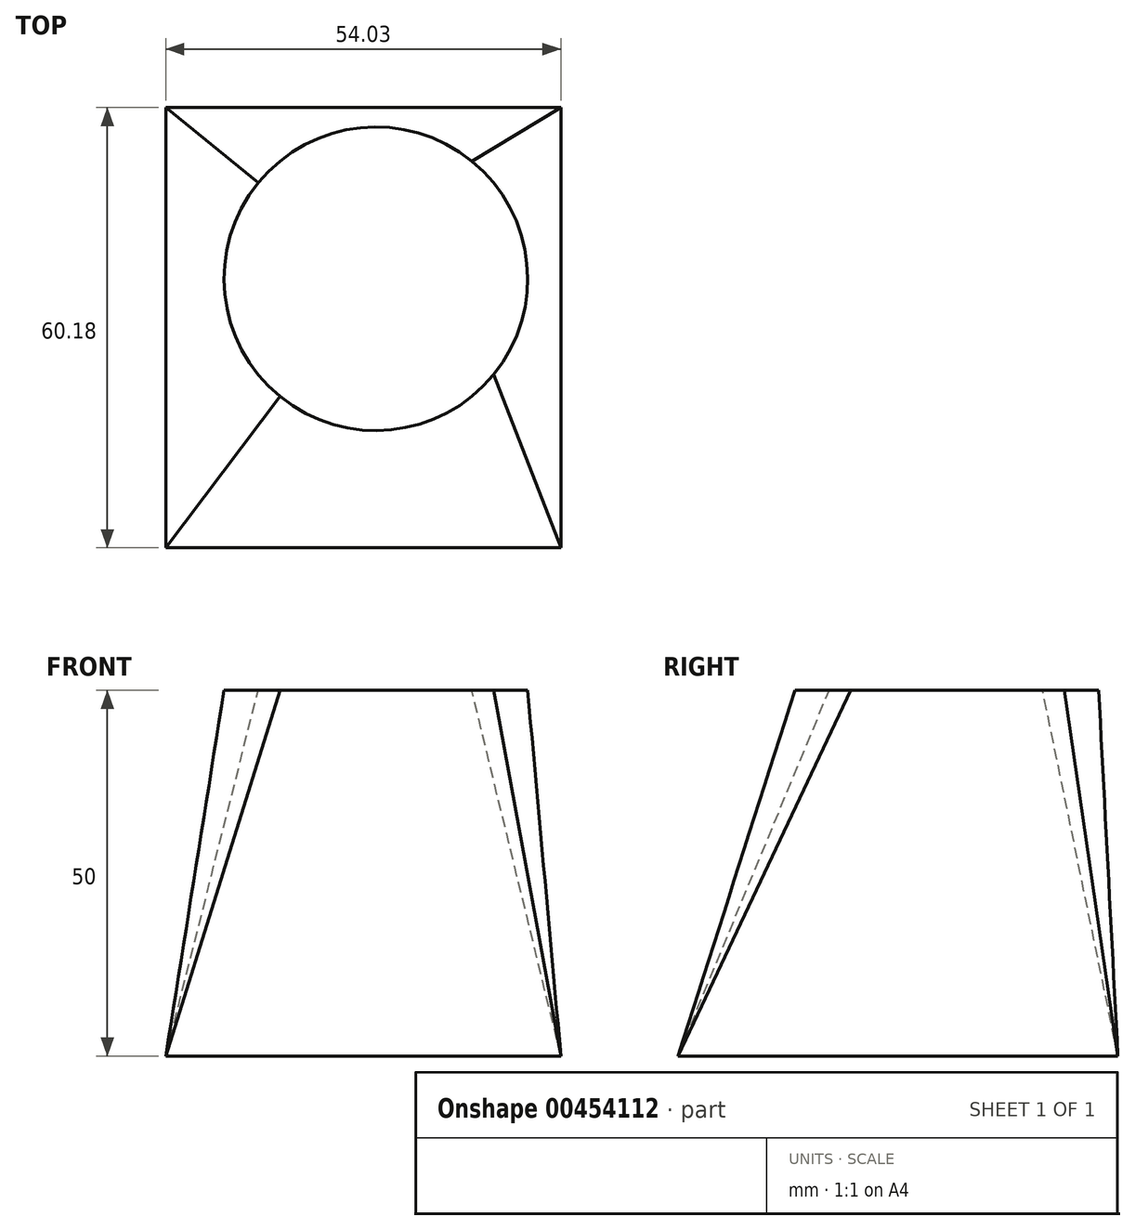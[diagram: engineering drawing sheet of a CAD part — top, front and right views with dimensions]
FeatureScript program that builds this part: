
annotation { "Feature Type Name" : "Feature", "Feature Type Description" : "" }
export const myFeature = defineFeature(function(context is Context, id is Id, definition is map)
    precondition{}
    {
        {
            var Q0;
            Q0=qCreatedBy(makeId("Top.planeOp"),FACE);
            var sketch = newSketch(context, id + "F0", { "sketchPlane" : qUnion([Q0])});
            skLineSegment(sketch, "E0.bottom", {"start": v(0, 0) * mm, "end": v(54.03, 0) * mm});
            skLineSegment(sketch, "E0.top", {"start": v(0, -60.18) * mm, "end": v(54.03, -60.18) * mm});
            skLineSegment(sketch, "E0.left", {"start": v(0, 0) * mm, "end": v(0, -60.18) * mm});
            skLineSegment(sketch, "E0.right", {"start": v(54.03, 0) * mm, "end": v(54.03, -60.18) * mm});
            skSolve(sketch);
        }
        {
            var Q0;
            Q0=qCreatedBy(makeId("Top.planeOp"),FACE);
            cPlane(context, id + "F1", {"entities" : qUnion([Q0]), "cplaneType" : CPlaneType.OFFSET, "offset" : 50 * mm, "width" : 150 * mm, "height" : 150 * mm});
        }
        {
            var Q0;
            Q0=qCreatedBy(id+"F1.planeOp",FACE);
            var sketch = newSketch(context, id + "F2", { "sketchPlane" : qUnion([Q0])});
            skCircle(sketch, "E1", {"center": v(28.72, -23.4) * mm, "radius": 20.76 * mm});
            skSolve(sketch);
        }
        {
            var Q0;
            Q0 = qSketchRegion(id + "F0", true);
            var Q1;
            Q1 = qSketchRegion(id + "F2", true);
            loft(context, id + "F3", {"sheetProfilesArray" : [{ "sheetProfileEntities" : qUnion([Q0]) }, { "sheetProfileEntities" : qUnion([Q1]) }]});
        }
    });
